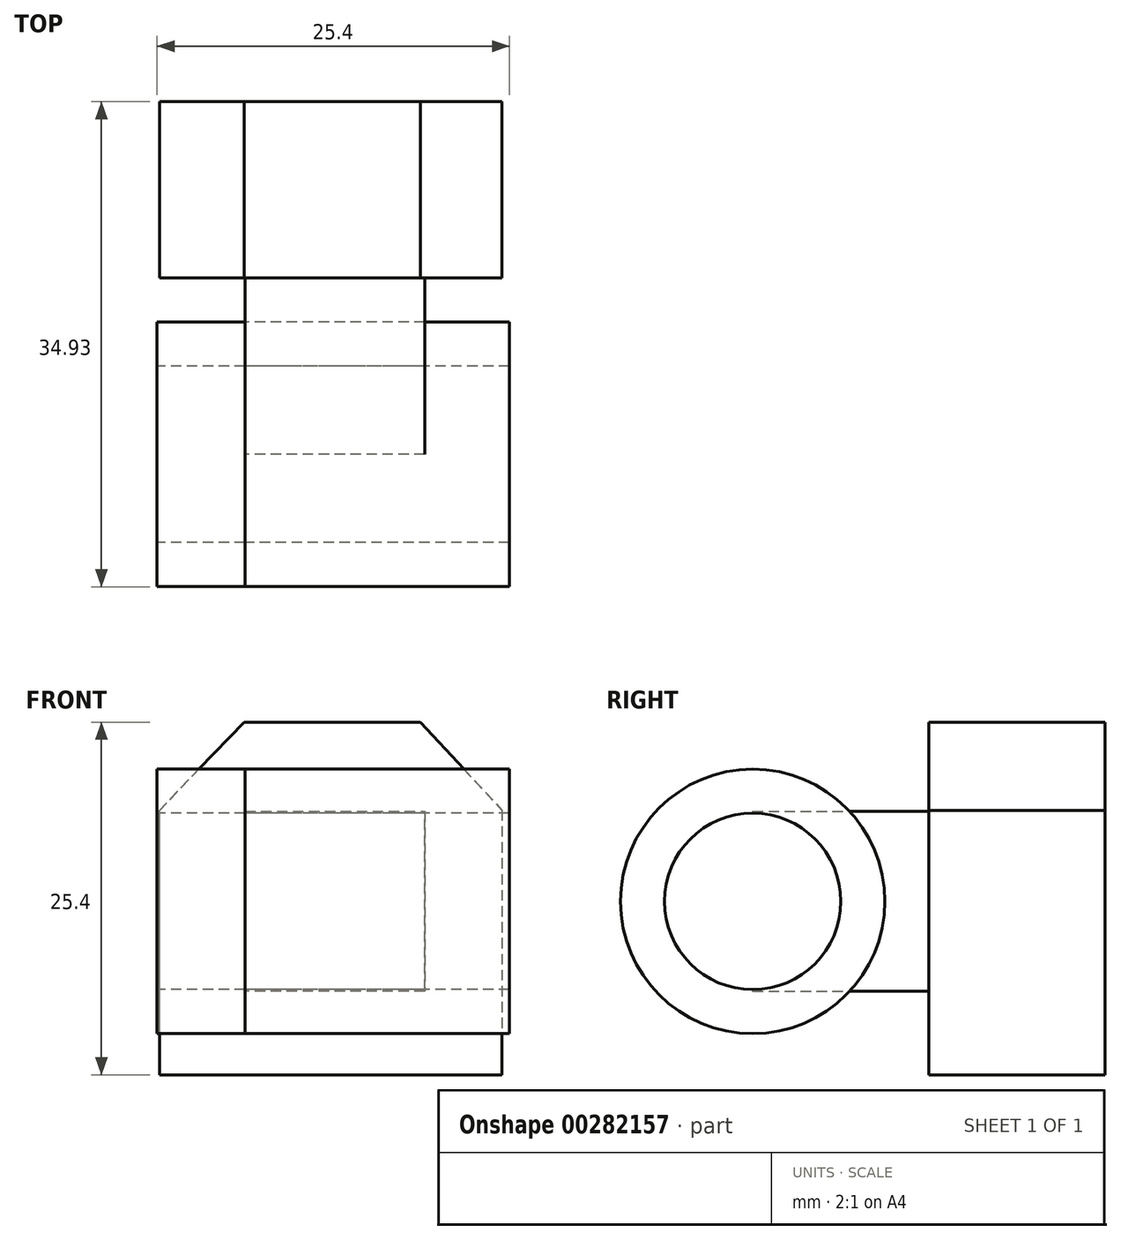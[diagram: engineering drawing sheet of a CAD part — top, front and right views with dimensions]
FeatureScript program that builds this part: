
annotation { "Feature Type Name" : "Feature", "Feature Type Description" : "" }
export const myFeature = defineFeature(function(context is Context, id is Id, definition is map)
    precondition{}
    {
        {
            var Q0;
            Q0=qCreatedBy(makeId("Front.planeOp"),FACE);
            var sketch = newSketch(context, id + "F0", { "sketchPlane" : qUnion([Q0])});
            skLineSegment(sketch, "E0", {"start": v(0, 0) * mm, "end": v(0, 19.05) * mm});
            skLineSegment(sketch, "E1", {"start": v(0, 19.05) * mm, "end": v(6.1, 19.05) * mm});
            skLineSegment(sketch, "E2", {"start": v(6.1, 19.05) * mm, "end": v(6.1, 25.4) * mm});
            skLineSegment(sketch, "E3", {"start": v(6.1, 25.4) * mm, "end": v(18.8, 25.4) * mm});
            skLineSegment(sketch, "E4", {"start": v(18.8, 25.4) * mm, "end": v(18.8, 19.05) * mm});
            skLineSegment(sketch, "E5", {"start": v(18.8, 19.05) * mm, "end": v(24.69, 19.05) * mm});
            skLineSegment(sketch, "E6", {"start": v(24.69, 19.05) * mm, "end": v(24.69, 0) * mm});
            skLineSegment(sketch, "E7", {"start": v(24.69, 0) * mm, "end": v(0, 0) * mm});
            skSolve(sketch);
        }
        {
            var Q0;
            Q0 = qSketchRegion(id + "F0", true);
            extrude(context, id + "F1", {"entities" : qUnion([Q0]), "depth" : 12.7 * mm});
        }
        {
            var Q0;
            Q0=makeQuery(id+"F1.opExtrude","CAP_FACE",FACE,{"disambiguationData":[OSD([sQuery(id+"F0.wireOp",EDGE,"E0"),sQuery(id+"F0.wireOp",EDGE,"E1"),sQuery(id+"F0.wireOp",EDGE,"E2"),sQuery(id+"F0.wireOp",EDGE,"E3"),sQuery(id+"F0.wireOp",EDGE,"E4"),sQuery(id+"F0.wireOp",EDGE,"E5"),sQuery(id+"F0.wireOp",EDGE,"E6"),sQuery(id+"F0.wireOp",EDGE,"E7")])],"isStart":false});
            var sketch = newSketch(context, id + "F2", { "sketchPlane" : qUnion([Q0])});
            skLineSegment(sketch, "E8", {"start": v(0, 19.05) * mm, "end": v(6.1, 19.05) * mm});
            skLineSegment(sketch, "E9", {"start": v(6.1, 19.05) * mm, "end": v(6.1, 25.4) * mm});
            skLineSegment(sketch, "E10", {"start": v(6.1, 25.4) * mm, "end": v(0, 19.05) * mm});
            skSolve(sketch);
        }
        {
            var Q0;
            Q0 = qSketchRegion(id + "F2", true);
            extrude(context, id + "F3", {"entities" : qUnion([Q0]), "operationType" : NewBodyOperationType.ADD, "oppositeDirection" : true, "depth" : 12.7 * mm});
        }
        {
            var Q0;
            Q0=makeQuery(id+"F3.boolean.opBoolean","MERGE",FACE,{"derivedFrom":[makeQuery(id+"F1.opExtrude","CAP_FACE",FACE,{"disambiguationData":[OSD([sQuery(id+"F0.wireOp",EDGE,"E0"),sQuery(id+"F0.wireOp",EDGE,"E1"),sQuery(id+"F0.wireOp",EDGE,"E2"),sQuery(id+"F0.wireOp",EDGE,"E3"),sQuery(id+"F0.wireOp",EDGE,"E4"),sQuery(id+"F0.wireOp",EDGE,"E5"),sQuery(id+"F0.wireOp",EDGE,"E6"),sQuery(id+"F0.wireOp",EDGE,"E7")])],"isStart":false}),makeQuery(id+"F3.opExtrude","CAP_FACE",FACE,{"disambiguationData":[OSD([sQuery(id+"F2.wireOp",EDGE,"E8"),sQuery(id+"F2.wireOp",EDGE,"E9"),sQuery(id+"F2.wireOp",EDGE,"E10")])],"isStart":true})]});
            var sketch = newSketch(context, id + "F4", { "sketchPlane" : qUnion([Q0])});
            skLineSegment(sketch, "E11", {"start": v(18.8, 25.4) * mm, "end": v(24.69, 19.05) * mm});
            skLineSegment(sketch, "E12", {"start": v(24.69, 19.05) * mm, "end": v(18.8, 19.05) * mm});
            skLineSegment(sketch, "E13", {"start": v(18.8, 19.05) * mm, "end": v(18.8, 25.4) * mm});
            skSolve(sketch);
        }
        {
            var Q0;
            Q0 = qSketchRegion(id + "F4", true);
            extrude(context, id + "F5", {"entities" : qUnion([Q0]), "operationType" : NewBodyOperationType.ADD, "oppositeDirection" : true, "depth" : 12.7 * mm});
        }
        {
            var Q0;
            Q0=makeQuery(id+"F5.boolean.opBoolean","MERGE",FACE,{"derivedFrom":[makeQuery(id+"F3.boolean.opBoolean","MERGE",FACE,{"derivedFrom":[makeQuery(id+"F1.opExtrude","CAP_FACE",FACE,{"disambiguationData":[OSD([sQuery(id+"F0.wireOp",EDGE,"E0"),sQuery(id+"F0.wireOp",EDGE,"E1"),sQuery(id+"F0.wireOp",EDGE,"E2"),sQuery(id+"F0.wireOp",EDGE,"E3"),sQuery(id+"F0.wireOp",EDGE,"E4"),sQuery(id+"F0.wireOp",EDGE,"E5"),sQuery(id+"F0.wireOp",EDGE,"E6"),sQuery(id+"F0.wireOp",EDGE,"E7")])],"isStart":false}),makeQuery(id+"F3.opExtrude","CAP_FACE",FACE,{"disambiguationData":[OSD([sQuery(id+"F2.wireOp",EDGE,"E8"),sQuery(id+"F2.wireOp",EDGE,"E9"),sQuery(id+"F2.wireOp",EDGE,"E10")])],"isStart":true})]}),makeQuery(id+"F5.opExtrude","CAP_FACE",FACE,{"disambiguationData":[OSD([sQuery(id+"F4.wireOp",EDGE,"E11"),sQuery(id+"F4.wireOp",EDGE,"E12"),sQuery(id+"F4.wireOp",EDGE,"E13")])],"isStart":true})]});
            var sketch = newSketch(context, id + "F6", { "sketchPlane" : qUnion([Q0])});
            skPoint(sketch, "E14.endSnap0", {"position": v(24.69, 9.53) * mm});
            skLineSegment(sketch, "E15", {"start": v(12.64, 18.96) * mm, "end": v(19.12, 18.96) * mm});
            skLineSegment(sketch, "E16", {"start": v(19.12, 18.96) * mm, "end": v(19.12, 6.01) * mm});
            skLineSegment(sketch, "E17", {"start": v(19.12, 6.01) * mm, "end": v(6.17, 6.01) * mm});
            skLineSegment(sketch, "E18", {"start": v(6.17, 6.01) * mm, "end": v(6.17, 18.96) * mm});
            skLineSegment(sketch, "E19", {"start": v(6.17, 18.96) * mm, "end": v(12.64, 18.96) * mm});
            skLineSegment(sketch, "E20", {"start": v(6.17, 18.96) * mm, "end": v(19.12, 18.96) * mm});
            skLineSegment(sketch, "E21", {"start": v(6.17, 18.96) * mm, "end": v(12.64, 8.79) * mm});
            skSolve(sketch);
        }
        {
            var Q0;
            Q0=makeQuery(id+"F6.imprint","IMPRINT",FACE,{"disambiguationData":[TD([[makeQuery(id+"F6.imprint","IMPRINT",EDGE,{"derivedFrom":sQuery(id+"F6.wireOp",EDGE,"E16")}),-1.0]])]});
            extrude(context, id + "F7", {"entities" : qUnion([Q0]), "operationType" : NewBodyOperationType.ADD, "depth" : 12.7 * mm});
        }
        {
            var Q0;
            Q0=makeQuery(id+"F7.opExtrude","SWEPT_FACE",FACE,{"disambiguationData":[OSD([sQuery(id+"F6.wireOp",EDGE,"E18")])]});
            var sketch = newSketch(context, id + "F8", { "sketchPlane" : qUnion([Q0])});
            skCircle(sketch, "E22", {"center": v(25.4, 12.49) * mm, "radius": 9.53 * mm});
            skSolve(sketch);
        }
        {
            var Q0;
            Q0 = qSketchRegion(id + "F8", true);
            extrude(context, id + "F9", {"entities" : qUnion([Q0]), "oppositeDirection" : true, "depth" : 19.05 * mm});
        }
        {
            var Q0;
            Q0=makeQuery(id+"F9.opExtrude","CAP_FACE",FACE,{"disambiguationData":[OSD([sQuery(id+"F8.wireOp",EDGE,"E22")])],"isStart":true});
            extrude(context, id + "F10", {"entities" : qUnion([Q0]), "depth" : 6.35 * mm});
        }
        {
            var Q0;
            Q0=makeQuery(id+"F10.opExtrude","CAP_FACE",FACE,{"disambiguationData":[OSD([sQuery(id+"F8.wireOp",EDGE,"E22")])],"isStart":false});
            var sketch = newSketch(context, id + "F11", { "sketchPlane" : qUnion([Q0])});
            skCircle(sketch, "E23", {"center": v(25.4, 12.49) * mm, "radius": 6.35 * mm});
            skSolve(sketch);
        }
        {
            var Q0;
            Q0 = qSketchRegion(id + "F11", true);
            extrude(context, id + "F12", {"entities" : qUnion([Q0]), "operationType" : NewBodyOperationType.REMOVE, "oppositeDirection" : true, "depth" : 25.4 * mm});
        }
        {
            var Q0;
            Q0=makeQuery(id+"F9.opExtrude","CAP_FACE",FACE,{"disambiguationData":[OSD([sQuery(id+"F8.wireOp",EDGE,"E22")])],"isStart":false});
            var sketch = newSketch(context, id + "F13", { "sketchPlane" : qUnion([Q0])});
            skCircle(sketch, "E24", {"center": v(-25.4, 12.49) * mm, "radius": 6.35 * mm});
            skSolve(sketch);
        }
        {
            var Q0;
            Q0 = qSketchRegion(id + "F13", true);
            extrude(context, id + "F14", {"entities" : qUnion([Q0]), "operationType" : NewBodyOperationType.REMOVE, "oppositeDirection" : true, "depth" : 25.4 * mm});
        }
    });
